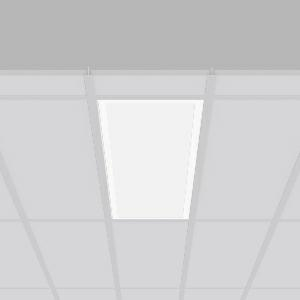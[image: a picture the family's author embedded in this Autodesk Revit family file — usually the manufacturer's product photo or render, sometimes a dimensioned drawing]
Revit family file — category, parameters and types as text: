
# Revit family: sidelite_eco_672378_002_04_2a69
name_source: partatom
category: Lighting Fixtures
units: mm (PartAtom-declared; Revit-internal decimal feet)

## family parameters
Cut with Voids When Loaded = No
Host = Face
Light Source = No
Part Type = Normal
Room Calculation Point = No
Round Connector Dimension = Use Diameter
Shared = No

## types (1)
- SIDELITE ECO (1 x LED Modul 830, 3300 lm, 3000)
    Apparent Load = 29 VA
    CIE Flux Codes = 47 79 96 100 100
    Color Rendering = 80
    Color Temperature = 3000
    Default Elevation = 1800 mm
    Description = Series: SIDELITE ECO
Highly economical recessed luminaire with progressive LED technology. For escape route illumination. Frame made of aluminium, powder-coated. Diffuser: plastic, opal. Lightguide and diffuser made of non-yellowing plastic (PMMA). Lateral light emission (RZB SIDELITE technology) for homogeneous light distribution. External driver. Self-contained system with automatic self-test and feedback to the RZB monitoring system MULTIDIGIT. External driver with simple plug-in locking system. Extended connection cable (1.90 m). 
Colour: white
Length: 1245 mm
Width: 308 mm
Cut-out length: 1220 mm
Cut-out width: 285 mm
Recess height: 160 mm
Luminaire: recess height: 40 mm
Weight: 4.7 kg
Operating mode: maintained power mode
Duration time: 8 h
Lamp: LED
Socket: without socket
Colour temperature: 3000K
Colour rendering index (CRI): 80
System power: 29 W
Rated luminous flux: 3300 lm
Luminous flux, emergency: 220 lm
System power, emergency: -
Control gear: Regulated power supply
Protection class: I
Type of protection: IP 40
    Height = 0 mm  [stored 0 ft]
    Lamp = 1 x LED Modul 830
    Lamp Light Flux = 3300 lm
    Lamp count = 1
    Length = 1245 mm
    Lifetime = 50000 h
    Luminous efficacy = 114 lm/W
    Manufacturer = RZB
    ModVariant = No
    Model = 672378.002.04
    Mounting Place = Ceiling
    Mounting Type = Recessed
    Number of Poles = 1
    OnlyDefault = Yes
    Power Factor = 1
    Product Name = SIDELITE ECO
    Product group = Recessed modular luminaires
    ProductGroupID = 406
    Protection Class = Protection class I
    Protection Degree = IP 40
    RLX_Detail_Level = 1
    RLX_Emergency_Light_Flux = 220 lm
    RLX_Emergency_Type = 3
    RLX_Emergency_Type_DB = Yes
    RlxData = <blob elided: 30089 chars, md5=9c6e0f51>
    Socket = socket
    Standby Power = 0 W
    System Light Flux = 3300 lm
    System Power = 29 W
    Type Comments = Product without accessories
    Type Image = 312367.002.jpg
    URL = http://relux.com
    VarID = ---
    Voltage = 230 V
    Voltage Range = 220-240 V
    Weight = 0.00 kg
    Width = 308 mm

note: [stored X ft] marks values corroborated as IEEE doubles in the binary element streams (Revit-internal decimal feet)

## geometry (parser evidence)
native form markers: Blend x4, Sweep x12
no freeform markers — native parametric forms only
